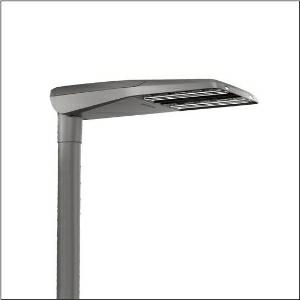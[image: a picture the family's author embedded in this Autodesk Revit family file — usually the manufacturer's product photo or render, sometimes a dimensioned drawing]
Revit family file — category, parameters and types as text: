
# Revit family: streetlight_sl_11_iq_midi___pc-l_5xc3e21f08me_5a59
name_source: partatom
category: Lighting Fixtures
units: mm (PartAtom-declared; Revit-internal decimal feet)

## family parameters
Cut with Voids When Loaded = No
Host = Face
Light Source = No
Part Type = Normal
Room Calculation Point = No
Round Connector Dimension = Use Diameter
Shared = No

## types (1)
- --- (1 x LED, 12740 lm, 124.7 W, 2200K)
    Apparent Load = 125 VA
    CIE Flux Codes = 37 73 96 100 100
    Color Rendering = 70
    Color Temperature = 2200K
    Default Elevation = 1800 mm
    Description = Streetlight SL 11 iQ midi, mast luminaire, primary light control with 3 zone facetted reflector, of plastic, silver coated, highly specular, primary optical cover: cover, of PMMA, transparent, light distribution: PC-L, light emission: direct distribution, primary light characteristic: asymmetric, installation type: post-top, side-entry, LED, High Power LED, rated luminous flux: 12.860lm, luminous efficacy: 103lm/W, light colour: 722, colour temperature: 2200K, control: Street-Remote, optimised constant luminous flux control (CLO 2.0), Desk-Remote (wireless, voltage-free reading and setting of iQ features in the workshop via application-optimized NFC function/RFID function), Light-Fading, Smart-Wire, Night-Set, Lumen-Switch, Temp-Guard, Auto-Match, with cable H07RN-F 5x 1.5mm², mains connection: 220..240V, AC, 50/60Hz, connection cable pre-assembled, cable length: 12,5m, start of lifetime: 125W, end of lifetime: 132W, reduction: 57W, luminaire housing, of diecast aluminium, powder-coated, Siteco® metallic grey (DB 702S), length: 780mm, width: 376mm, height: 118mm, spigot size: 60/76mm (post-top) and 42/60/76mm (side-entry), mast flange for spigot size: 42mm: 5XC10008XM4, 60mm: 5XC10008XM2, 76/60mm: 5XC10108XM1, equipment: Power, protection rating (complete): IP66, insulation class (complete): insulation class II (safety insulation), certification: CE, ENEC, VDE, impact resistance: IK09, permissible operating ambient temperature for outdoor applications: -25..+50°C, standard-compliant lighting for roads and squares, packaging unit: 1 piece

Light Distribution: PC-L
    Height = 118 mm
    Lamp = 1 x LED
    Lamp Light Flux = 12740 lm
    Lamp Power = 124.7 W
    Lamp count = 1
    Length = 780 mm
    Luminous efficacy = 102 lm/W
    Manufacturer = Siteco
    ModVariant = No
    Model = 5XC3E21F08ME
    Number of Poles = 1
    OnlyDefault = Yes
    Power Factor = 1
    Product Name = Streetlight SL 11 iQ midi | PC-L
    Product group = mast luminaire | pylon top
    ProductGroupID = 6100
    Protection Class = Protection class II
    Protection Degree = IP 66
    RLX_Detail_Level = 1
    RlxData = <blob elided: 74285 chars, md5=68890140>
    Socket = socket
    Standby Power = 0 W
    System Light Flux = 12741 lm
    System Power = 125 W
    Type Comments = factory setting: luminous flux: 100 % | dim-lin: 254 | 557 mA
    Type Image = l_1005960.jpg
    URL = http://relux.com
    VarID = @adj_036935
    Voltage = 0 V
    Weight = 0.00 kg
    Width = 376 mm

## geometry (parser evidence)
native form markers: Blend x4, Sweep x9
no freeform markers — native parametric forms only
